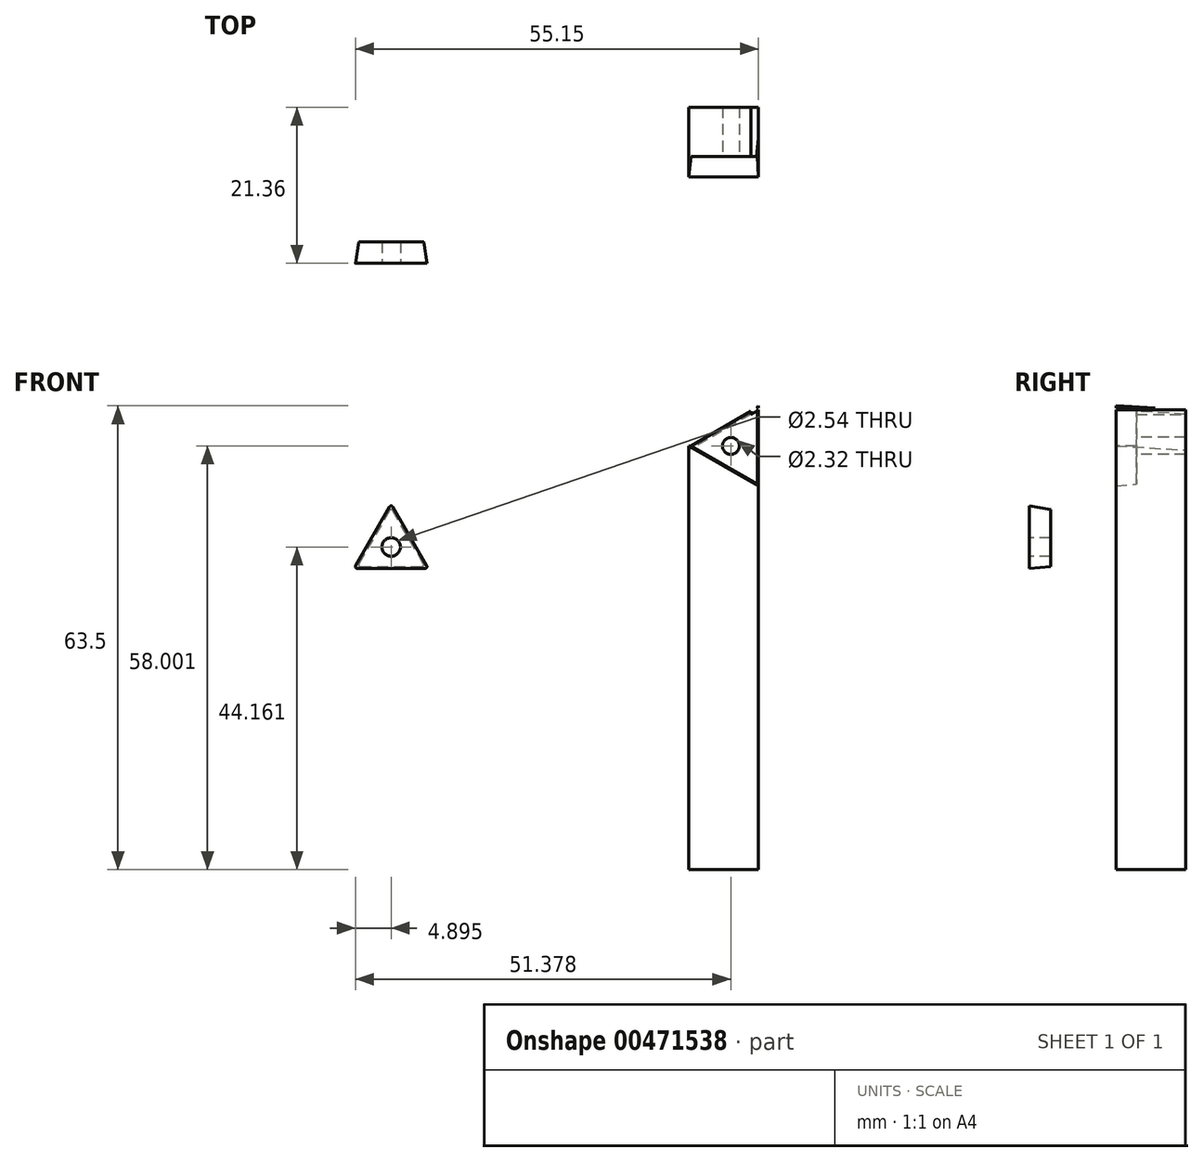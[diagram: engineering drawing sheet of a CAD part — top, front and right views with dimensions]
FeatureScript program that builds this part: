
annotation { "Feature Type Name" : "Feature", "Feature Type Description" : "" }
export const myFeature = defineFeature(function(context is Context, id is Id, definition is map)
    precondition{}
    {
        {
            var Q0;
            Q0=qCreatedBy(makeId("Top.planeOp"),FACE);
            var sketch = newSketch(context, id + "F0", { "sketchPlane" : qUnion([Q0])});
            skLineSegment(sketch, "E0.bottom", {"start": v(-9.53, 21.36) * mm, "end": v(0, 21.36) * mm});
            skLineSegment(sketch, "E0.top", {"start": v(-9.53, 11.84) * mm, "end": v(0, 11.84) * mm});
            skLineSegment(sketch, "E0.left", {"start": v(-9.53, 21.36) * mm, "end": v(-9.53, 11.84) * mm});
            skLineSegment(sketch, "E0.right", {"start": v(0, 21.36) * mm, "end": v(0, 11.84) * mm});
            skSolve(sketch);
        }
        {
            var Q0;
            Q0=makeQuery(id+"F0.imprint","IMPRINT",FACE,{"disambiguationData":[TD([[makeQuery(id+"F0.imprint","IMPRINT",EDGE,{"derivedFrom":sQuery(id+"F0.wireOp",EDGE,"E0.bottom")}),-1.0]])]});
            extrude(context, id + "F1", {"entities" : qUnion([Q0]), "depth" : 63.5 * mm});
        }
        {
            var Q0;
            Q0=makeQuery(id+"F1.opExtrude","SWEPT_FACE",FACE,{"disambiguationData":[OSD([sQuery(id+"F0.wireOp",EDGE,"E0.top")])]});
            var sketch = newSketch(context, id + "F2", { "sketchPlane" : qUnion([Q0])});
            skLineSegment(sketch, "E1", {"start": v(0, 63.5) * mm, "end": v(-9.52, 58) * mm});
            skLineSegment(sketch, "E2", {"start": v(-9.53, 58) * mm, "end": v(0, 52.5) * mm});
            skLineSegment(sketch, "E3", {"start": v(0, 52.5) * mm, "end": v(0, 63.5) * mm});
            skSolve(sketch);
        }
        {
            var Q0;
            {var subQ0=sQuery(id+"F2.wireOp",EDGE,"E1");Q0=makeQuery(id+"F2.imprint","IMPRINT",FACE,{"disambiguationData":[TD([[makeQuery(id+"F2.imprint","IMPRINT",EDGE,{"derivedFrom":subQ0}),-1.0]])]});}
            extrude(context, id + "F3", {"entities" : qUnion([Q0]), "operationType" : NewBodyOperationType.REMOVE, "oppositeDirection" : true, "depth" : 25.4 * mm, "hasDraft" : true, "draftAngle" : 3 * degree});
        }
        {
            var Q0;
            Q0 = qSketchRegion(id + "F2", true);
            extrude(context, id + "F4", {"entities" : qUnion([Q0]), "operationType" : NewBodyOperationType.REMOVE, "oppositeDirection" : true, "depth" : 2.8 * mm, "hasDraft" : true, "draftAngle" : 3 * degree, "draftPullDirection" : true});
        }
        {
            var Q0;
            Q0=makeQuery(id+"F1.opExtrude","SWEPT_FACE",FACE,{"disambiguationData":[OSD([sQuery(id+"F0.wireOp",EDGE,"E0.bottom")])]});
            var sketch = newSketch(context, id + "F5", { "sketchPlane" : qUnion([Q0])});
            skLineSegment(sketch, "E4.top", {"start": v(0, 53.02) * mm, "end": v(1.04, 53.02) * mm});
            skLineSegment(sketch, "E4.right", {"start": v(1.04, 63.18) * mm, "end": v(1.04, 53.02) * mm});
            skLineSegment(sketch, "E5.bottom", {"start": v(-0.23, 63.18) * mm, "end": v(1.04, 63.18) * mm});
            skLineSegment(sketch, "E5.top", {"start": v(-0.23, 53.02) * mm, "end": v(1.04, 53.02) * mm});
            skLineSegment(sketch, "E5.left", {"start": v(-0.23, 63.18) * mm, "end": v(-0.23, 53.02) * mm});
            skSolve(sketch);
        }
        {
            var Q0;
            {var subQ1=sQuery(id+"F5.wireOp",EDGE,"E5.bottom");Q0=makeQuery(id+"F5.imprint","IMPRINT",FACE,{"disambiguationData":[TD([[makeQuery(id+"F5.imprint","IMPRINT",EDGE,{"derivedFrom":subQ1}),-1.0]])]});}
            extrude(context, id + "F6", {"entities" : qUnion([Q0]), "operationType" : NewBodyOperationType.REMOVE, "depth" : 25.4 * mm});
        }
        {
            var Q0;
            {var subQ0=sQuery(id+"F5.wireOp",EDGE,"E4.right");var subQ1=sQuery(id+"F5.wireOp",EDGE,"E5.top");var subQ2=makeQuery(id+"F5.imprint","INTERSECT",VERTEX,{"derivedFrom":[subQ1,subQ0]});Q0=makeQuery(id+"F5.imprint","IMPRINT",FACE,{"disambiguationData":[TD([[makeQuery(id+"F5.imprint","IMPRINT",EDGE,{"disambiguationData":[TD([[subQ2,1.0]])],"derivedFrom":subQ1}),1.0]])]});}
            var Q1;
            {var subQ1=sQuery(id+"F5.wireOp",EDGE,"E5.bottom");Q1=makeQuery(id+"F5.imprint","IMPRINT",FACE,{"disambiguationData":[TD([[makeQuery(id+"F5.imprint","IMPRINT",EDGE,{"derivedFrom":subQ1}),-1.0]])]});}
            extrude(context, id + "F7", {"entities" : qUnion([Q0, Q1]), "operationType" : NewBodyOperationType.REMOVE, "oppositeDirection" : true, "depth" : 25.4 * mm});
        }
        {
            var Q0;
            Q0=qCreatedBy(makeId("Front.planeOp"),FACE);
            var sketch = newSketch(context, id + "F8", { "sketchPlane" : qUnion([Q0])});
            skLineSegment(sketch, "E6", {"start": v(-50.25, 50.03) * mm, "end": v(-55.33, 41.23) * mm});
            skLineSegment(sketch, "E7", {"start": v(-55.33, 41.23) * mm, "end": v(-45.17, 41.23) * mm});
            skLineSegment(sketch, "E8", {"start": v(-45.17, 41.23) * mm, "end": v(-50.25, 50.03) * mm});
            skSolve(sketch);
        }
        {
            var Q0;
            Q0=makeQuery(id+"F8.imprint","IMPRINT",FACE,{"disambiguationData":[TD([[makeQuery(id+"F8.imprint","IMPRINT",EDGE,{"derivedFrom":sQuery(id+"F8.wireOp",EDGE,"E6")}),1.0]])]});
            extrude(context, id + "F9", {"entities" : qUnion([Q0]), "oppositeDirection" : true, "depth" : 2.9 * mm, "hasDraft" : true, "draftAngle" : 5 * degree, "draftPullDirection" : true});
        }
        {
            var Q0;
            Q0=makeQuery(id+"F9.opExtrude","CAP_FACE",FACE,{"disambiguationData":[OSD([sQuery(id+"F8.wireOp",EDGE,"E6"),sQuery(id+"F8.wireOp",EDGE,"E7"),sQuery(id+"F8.wireOp",EDGE,"E8")])],"isStart":true});
            var sketch = newSketch(context, id + "F10", { "sketchPlane" : qUnion([Q0])});
            skLineSegment(sketch, "E9", {"start": v(-47.71, 45.63) * mm, "end": v(-55.33, 41.23) * mm, "construction": true});
            skLineSegment(sketch, "E10", {"start": v(-52.8, 45.63) * mm, "end": v(-45.17, 41.23) * mm, "construction": true});
            skCircle(sketch, "E11", {"center": v(-50.25, 44.16) * mm, "radius": 1.27 * mm});
            skSolve(sketch);
        }
        {
            var Q0;
            Q0=makeQuery(id+"F10.imprint","IMPRINT",FACE,{"disambiguationData":[TD([[makeQuery(id+"F10.imprint","IMPRINT",EDGE,{"derivedFrom":sQuery(id+"F10.wireOp",EDGE,"E11")}),1.0]])]});
            extrude(context, id + "F11", {"entities" : qUnion([Q0]), "operationType" : NewBodyOperationType.REMOVE, "oppositeDirection" : true, "depth" : 25.4 * mm});
        }
        {
            var Q0;
            Q0=makeQuery(id+"F9.opExtrude","SWEPT_EDGE",EDGE,{"disambiguationData":[OSD([sQuery(id+"F8.wireOp",EDGE,"E6"),sQuery(id+"F8.wireOp",EDGE,"E8")])]});
            var Q1;
            Q1=makeQuery(id+"F9.opExtrude","SWEPT_EDGE",EDGE,{"disambiguationData":[OSD([sQuery(id+"F8.wireOp",EDGE,"E6"),sQuery(id+"F8.wireOp",EDGE,"E7")])]});
            var Q2;
            Q2=makeQuery(id+"F9.opExtrude","SWEPT_EDGE",EDGE,{"disambiguationData":[OSD([sQuery(id+"F8.wireOp",EDGE,"E7"),sQuery(id+"F8.wireOp",EDGE,"E8")])]});
            fillet(context, id + "F12", {"entities" : qUnion([Q0, Q1, Q2]), "radius" : 0.25 * mm, "tangentPropagation" : true, "allowEdgeOverflow" : false});
        }
        {
            var Q0;
            Q0=qCreatedBy(makeId("Front.planeOp"),FACE);
            var sketch = newSketch(context, id + "F13", { "sketchPlane" : qUnion([Q0])});
            skLineSegment(sketch, "E12.0.0", {"start": v(-9.23, 58) * mm, "end": v(-1.04, 53.27) * mm});
            skLineSegment(sketch, "E12.0.1", {"start": v(-1.04, 53.27) * mm, "end": v(-1.04, 62.73) * mm});
            skLineSegment(sketch, "E12.0.2", {"start": v(-1.04, 62.73) * mm, "end": v(-9.23, 58) * mm});
            skLineSegment(sketch, "E13", {"start": v(-9.23, 58) * mm, "end": v(-1.04, 58) * mm, "construction": true});
            skLineSegment(sketch, "E14", {"start": v(-1.04, 53.27) * mm, "end": v(-4.86, 59.9) * mm, "construction": true});
            skCircle(sketch, "E15", {"center": v(-3.77, 58) * mm, "radius": 1.16 * mm});
            skSolve(sketch);
        }
        {
            var Q0;
            Q0=makeQuery(id+"F13.imprint","IMPRINT",FACE,{"disambiguationData":[TD([[makeQuery(id+"F13.imprint","IMPRINT",EDGE,{"derivedFrom":sQuery(id+"F13.wireOp",EDGE,"E15")}),1.0]])]});
            extrude(context, id + "F14", {"entities" : qUnion([Q0]), "operationType" : NewBodyOperationType.REMOVE, "oppositeDirection" : true, "depth" : 25.4 * mm});
        }
        {
            var Q0;
            {var subQ0=sQuery(id+"F5.wireOp",EDGE,"E5.top");var subQ8=sQuery(id+"F5.wireOp",EDGE,"E4.right");var subQ9=makeQuery(id+"F5.imprint","INTERSECT",VERTEX,{"derivedFrom":[subQ0,subQ8]});Q0=makeQuery(id+"F5.imprint","IMPRINT",FACE,{"disambiguationData":[TD([[makeQuery(id+"F5.imprint","IMPRINT",EDGE,{"disambiguationData":[TD([[subQ9,1.0]])],"derivedFrom":subQ0}),1.0]])]});}
            extrude(context, id + "F15", {"entities" : qUnion([Q0]), "operationType" : NewBodyOperationType.REMOVE, "oppositeDirection" : true, "depth" : 25.4 * mm});
        }
    });
